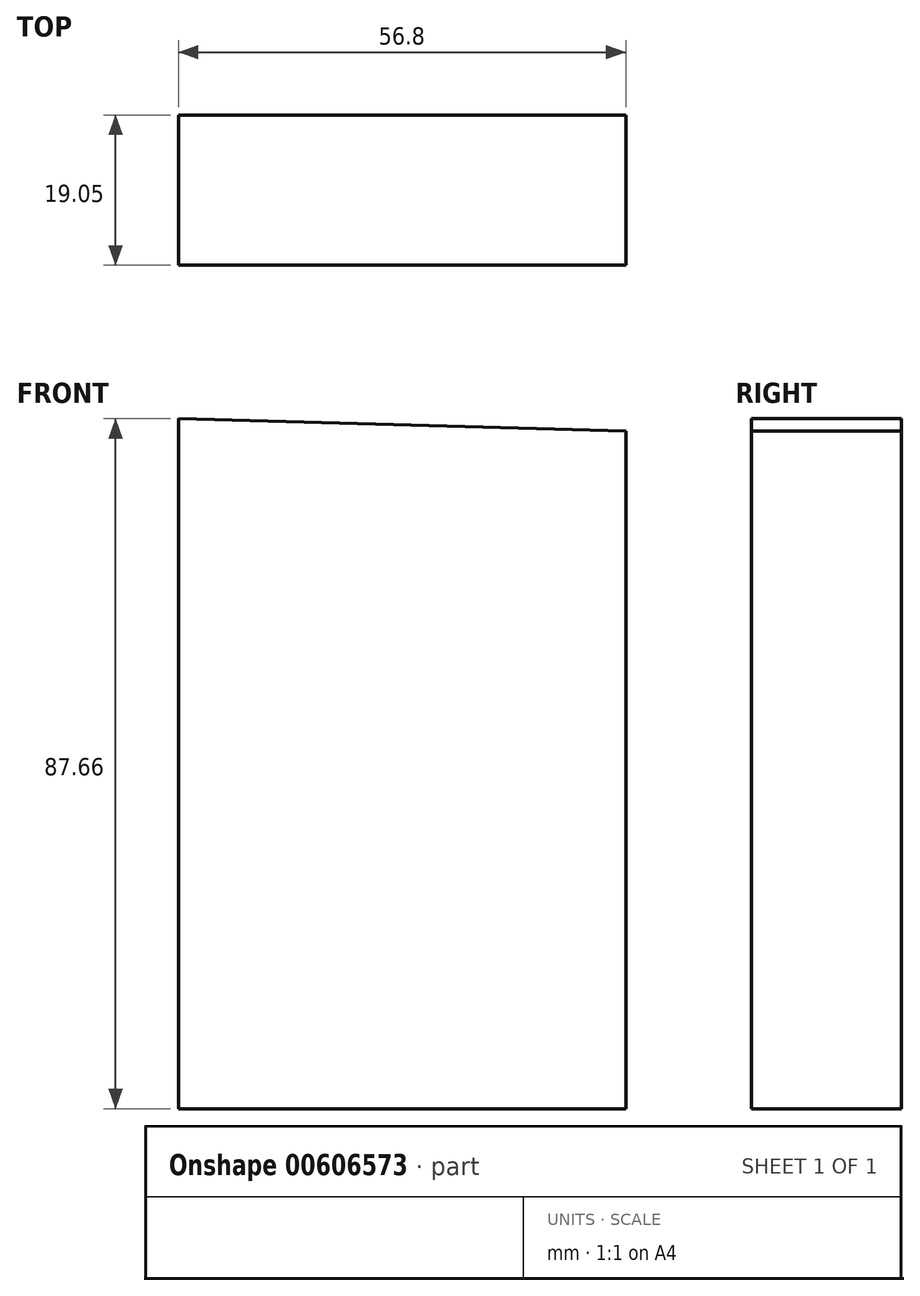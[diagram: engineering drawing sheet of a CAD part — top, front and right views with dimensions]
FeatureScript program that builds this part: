
annotation { "Feature Type Name" : "Feature", "Feature Type Description" : "" }
export const myFeature = defineFeature(function(context is Context, id is Id, definition is map)
    precondition{}
    {
        {
            var Q0;
            Q0=qCreatedBy(makeId("Front.planeOp"),FACE);
            var sketch = newSketch(context, id + "F0", { "sketchPlane" : qUnion([Q0])});
            skLineSegment(sketch, "E0", {"start": v(-73.4, 37.09) * mm, "end": v(-73.4, -50.57) * mm});
            skLineSegment(sketch, "E1", {"start": v(-73.4, -50.57) * mm, "end": v(-16.6, -50.57) * mm});
            skLineSegment(sketch, "E2", {"start": v(-16.6, -50.57) * mm, "end": v(-16.6, 35.53) * mm});
            skLineSegment(sketch, "E3", {"start": v(-16.6, 35.53) * mm, "end": v(-73.4, 37.09) * mm});
            skSolve(sketch);
        }
        {
            var Q0;
            Q0=makeQuery(id+"F0.imprint","IMPRINT",FACE,{"disambiguationData":[TD([[makeQuery(id+"F0.imprint","IMPRINT",EDGE,{"derivedFrom":sQuery(id+"F0.wireOp",EDGE,"E0")}),1.0]])]});
            extrude(context, id + "F1", {"entities" : qUnion([Q0]), "depth" : 19.05 * mm, "offsetDistance" : 25.4 * mm});
        }
    });
